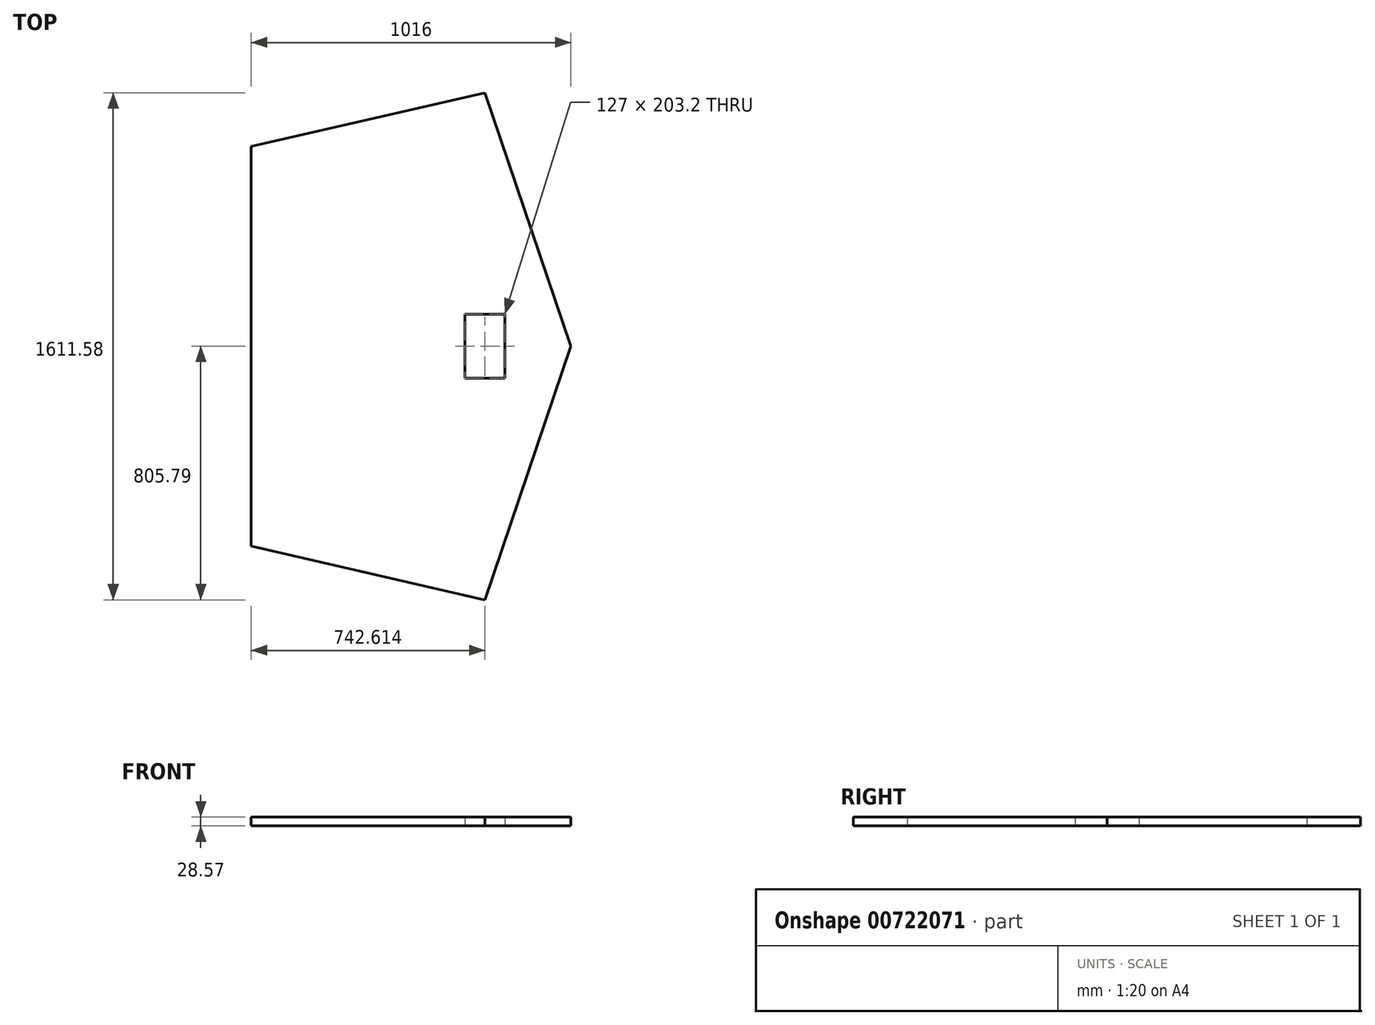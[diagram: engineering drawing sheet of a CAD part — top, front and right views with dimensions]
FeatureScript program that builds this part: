
annotation { "Feature Type Name" : "Feature", "Feature Type Description" : "" }
export const myFeature = defineFeature(function(context is Context, id is Id, definition is map)
    precondition{}
    {
        {
            var Q0;
            Q0=qCreatedBy(makeId("Top.planeOp"),FACE);
            var sketch = newSketch(context, id + "F0", { "sketchPlane" : qUnion([Q0])});
            skLineSegment(sketch, "E0.0", {"start": v(571.5, 0) * mm, "end": v(298.11, -805.79) * mm});
            skLineSegment(sketch, "E0.1", {"start": v(298.11, -805.79) * mm, "end": v(-444.5, -635) * mm});
            skLineSegment(sketch, "E0.2", {"start": v(-444.5, -635) * mm, "end": v(-444.5, 635) * mm});
            skLineSegment(sketch, "E0.3", {"start": v(-444.5, 635) * mm, "end": v(298.11, 805.79) * mm});
            skLineSegment(sketch, "E0.4", {"start": v(298.11, 805.79) * mm, "end": v(571.5, 0) * mm});
            skLineSegment(sketch, "E1", {"start": v(571.5, 0) * mm, "end": v(-444.5, 0) * mm});
            skLineSegment(sketch, "E2", {"start": v(298.11, 805.79) * mm, "end": v(298.11, 0) * mm});
            skLineSegment(sketch, "E3", {"start": v(298.11, 0) * mm, "end": v(298.11, -805.79) * mm});
            skLineSegment(sketch, "E4.bottom", {"start": v(63.5, 101.6) * mm, "end": v(-63.5, 101.6) * mm});
            skLineSegment(sketch, "E4.top", {"start": v(63.5, -101.6) * mm, "end": v(-63.5, -101.6) * mm});
            skLineSegment(sketch, "E4.left", {"start": v(63.5, 101.6) * mm, "end": v(63.5, -101.6) * mm});
            skLineSegment(sketch, "E4.right", {"start": v(-63.5, 101.6) * mm, "end": v(-63.5, -101.6) * mm});
            skPoint(sketch, "E4.middle", {"position": v(0, 0) * mm});
            skPoint(sketch, "E4.cornerSnap0", {"position": v(63.5, 0) * mm});
            skLineSegment(sketch, "E5.bottom", {"start": v(361.61, 101.6) * mm, "end": v(234.61, 101.6) * mm});
            skLineSegment(sketch, "E5.top", {"start": v(361.61, -101.6) * mm, "end": v(234.61, -101.6) * mm});
            skLineSegment(sketch, "E5.left", {"start": v(361.61, 101.6) * mm, "end": v(361.61, -101.6) * mm});
            skLineSegment(sketch, "E5.right", {"start": v(234.61, 101.6) * mm, "end": v(234.61, -101.6) * mm});
            skPoint(sketch, "E5.middle", {"position": v(298.11, 0) * mm});
            skSolve(sketch);
        }
        {
            var Q0;
            Q0=makeQuery(id+"F0.imprint","IMPRINT",FACE,{"disambiguationData":[TD([[makeQuery(id+"F0.imprint","IMPRINT",EDGE,{"derivedFrom":sQuery(id+"F0.wireOp",EDGE,"E0.0")}),-1.0]])]});
            var Q1;
            {var subQ0=sQuery(id+"F0.wireOp",EDGE,"E0.3");Q1=makeQuery(id+"F0.imprint","IMPRINT",FACE,{"disambiguationData":[TD([[makeQuery(id+"F0.imprint","IMPRINT",EDGE,{"derivedFrom":subQ0}),-1.0]])]});}
            var Q2;
            {var subQ0=sQuery(id+"F0.wireOp",EDGE,"E0.4");Q2=makeQuery(id+"F0.imprint","IMPRINT",FACE,{"disambiguationData":[TD([[makeQuery(id+"F0.imprint","IMPRINT",EDGE,{"derivedFrom":subQ0}),-1.0]])]});}
            var Q3;
            {var subQ0=sQuery(id+"F0.wireOp",EDGE,"E0.1");Q3=makeQuery(id+"F0.imprint","IMPRINT",FACE,{"disambiguationData":[TD([[makeQuery(id+"F0.imprint","IMPRINT",EDGE,{"derivedFrom":subQ0}),-1.0]])]});}
            var Q4;
            {var subQ5=sQuery(id+"F0.wireOp",EDGE,"E4.bottom");Q4=makeQuery(id+"F0.imprint","IMPRINT",FACE,{"disambiguationData":[TD([[makeQuery(id+"F0.imprint","IMPRINT",EDGE,{"derivedFrom":subQ5}),1.0]])]});}
            var Q5;
            {var subQ5=sQuery(id+"F0.wireOp",EDGE,"E4.top");Q5=makeQuery(id+"F0.imprint","IMPRINT",FACE,{"disambiguationData":[TD([[makeQuery(id+"F0.imprint","IMPRINT",EDGE,{"derivedFrom":subQ5}),-1.0]])]});}
            extrude(context, id + "F1", {"entities" : qUnion([Q0, Q1, Q2, Q3, Q4, Q5]), "depth" : 28.57 * mm, "offsetDistance" : 25.4 * mm});
        }
    });
